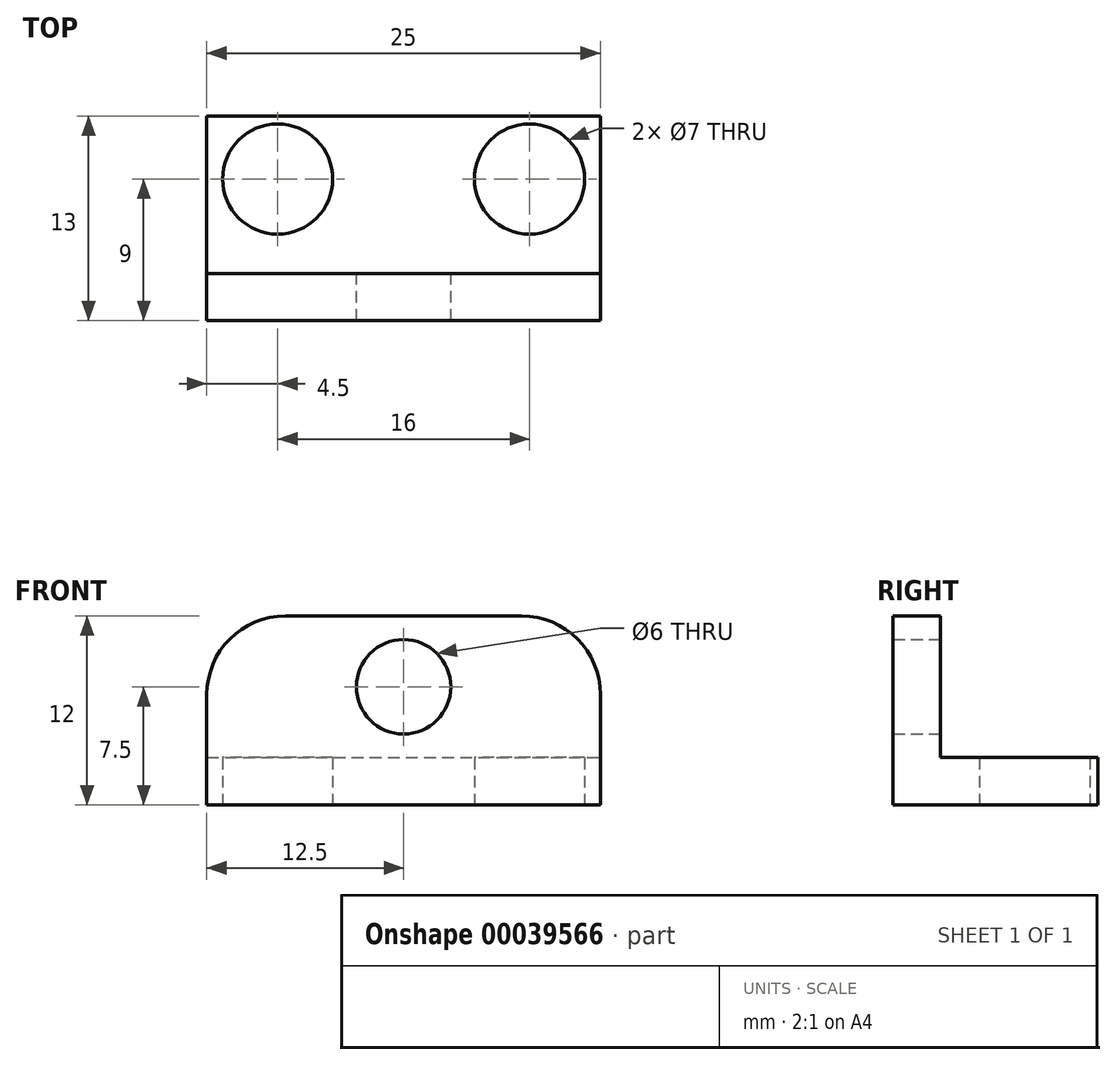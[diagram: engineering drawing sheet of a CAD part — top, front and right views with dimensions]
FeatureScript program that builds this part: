
annotation { "Feature Type Name" : "Feature", "Feature Type Description" : "" }
export const myFeature = defineFeature(function(context is Context, id is Id, definition is map)
    precondition{}
    {
        {
            var Q0;
            Q0=qCreatedBy(makeId("Top.planeOp"),FACE);
            var sketch = newSketch(context, id + "F0", { "sketchPlane" : qUnion([Q0])});
            skLineSegment(sketch, "E0.bottom", {"start": v(0, 0) * mm, "end": v(25, 0) * mm});
            skLineSegment(sketch, "E0.top", {"start": v(0, 10) * mm, "end": v(25, 10) * mm});
            skLineSegment(sketch, "E0.left", {"start": v(0, 0) * mm, "end": v(0, 10) * mm});
            skLineSegment(sketch, "E0.right", {"start": v(25, 0) * mm, "end": v(25, 10) * mm});
            skLineSegment(sketch, "E1", {"start": v(0, -4.44) * mm, "end": v(4.5, -4.44) * mm, "construction": true});
            skLineSegment(sketch, "E2", {"start": v(25, -4.44) * mm, "end": v(20.5, -4.44) * mm, "construction": true});
            skLineSegment(sketch, "E3", {"start": v(4.5, -4.44) * mm, "end": v(4.5, 10) * mm, "construction": true});
            skLineSegment(sketch, "E4", {"start": v(20.5, -4.44) * mm, "end": v(20.5, 10) * mm, "construction": true});
            skLineSegment(sketch, "E5", {"start": v(-3.35, 10) * mm, "end": v(-3.35, 6) * mm, "construction": true});
            skLineSegment(sketch, "E6", {"start": v(-3.35, 6) * mm, "end": v(25, 6) * mm, "construction": true});
            skCircle(sketch, "E7", {"center": v(4.5, 6) * mm, "radius": 3.5 * mm});
            skCircle(sketch, "E8", {"center": v(20.5, 6) * mm, "radius": 3.5 * mm});
            skSolve(sketch);
        }
        {
            var Q0;
            Q0=qSketchRegion(id+"F0",true);
            extrude(context, id + "F1", {"entities" : qUnion([Q0]), "depth" : 3 * mm});
        }
        {
            var Q0;
            Q0=makeQuery(id+"F1.opExtrude","SWEPT_FACE",FACE,{"disambiguationData":[OSD([sQuery(id+"F0.wireOp",EDGE,"E0.bottom")])]});
            var sketch = newSketch(context, id + "F2", { "sketchPlane" : qUnion([Q0])});
            skLineSegment(sketch, "E9.bottom", {"start": v(0, 0) * mm, "end": v(25, 0) * mm});
            skLineSegment(sketch, "E9.top", {"start": v(5, 12) * mm, "end": v(20, 12) * mm});
            skLineSegment(sketch, "E9.left", {"start": v(0, 0) * mm, "end": v(0, 7) * mm});
            skLineSegment(sketch, "E9.right", {"start": v(25, 0) * mm, "end": v(25, 7) * mm});
            skLineSegment(sketch, "E10", {"start": v(12.5, 12) * mm, "end": v(12.5, 7.5) * mm, "construction": true});
            skLineSegment(sketch, "E11", {"start": v(12.5, 7.5) * mm, "end": v(25, 7.5) * mm, "construction": true});
            skCircle(sketch, "E12", {"center": v(12.5, 7.5) * mm, "radius": 3 * mm});
            skPoint(sketch, "E13.visualSharp", {"position": v(0, 12) * mm});
            skArc(sketch, "E13.filletArc", {"start": v(5, 12) * mm, "mid": v(1.46, 10.54) * mm, "end": v(0, 7) * mm});
            skPoint(sketch, "E14.visualSharp", {"position": v(25, 12) * mm});
            skArc(sketch, "E14.filletArc", {"start": v(25, 7) * mm, "mid": v(23.54, 10.54) * mm, "end": v(20, 12) * mm});
            skSolve(sketch);
        }
        {
            var Q0;
            Q0=qSketchRegion(id+"F2",true);
            extrude(context, id + "F3", {"entities" : qUnion([Q0]), "operationType" : NewBodyOperationType.ADD, "depth" : 3 * mm});
        }
    });
